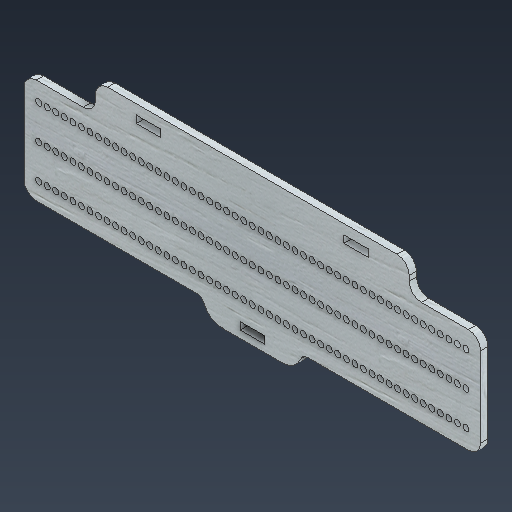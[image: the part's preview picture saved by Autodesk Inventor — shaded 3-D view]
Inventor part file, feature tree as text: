
AUTODESK INVENTOR PART (.ipt)
format: ipt  version: 2025.3 (Build 293356000, 356)  size: 515,584 bytes
history: native  units: mm
features: other x3, sketch x2, extrude x1
ambient origin geometry x8: Origin, YZ Plane, XZ Plane, XY Plane, X Axis, Y Axis, Z Axis, Center Point
bodies: Body1 (feature_tree)
feature tree (6):
  other  "實體1"
  extrude  "擠出1"  Depth=10.0mm
  sketch  "草圖3"
  sketch  "草圖1"
  other  "草圖 - 矩形陣列5"
  other  "草圖 - 矩形陣列12"
